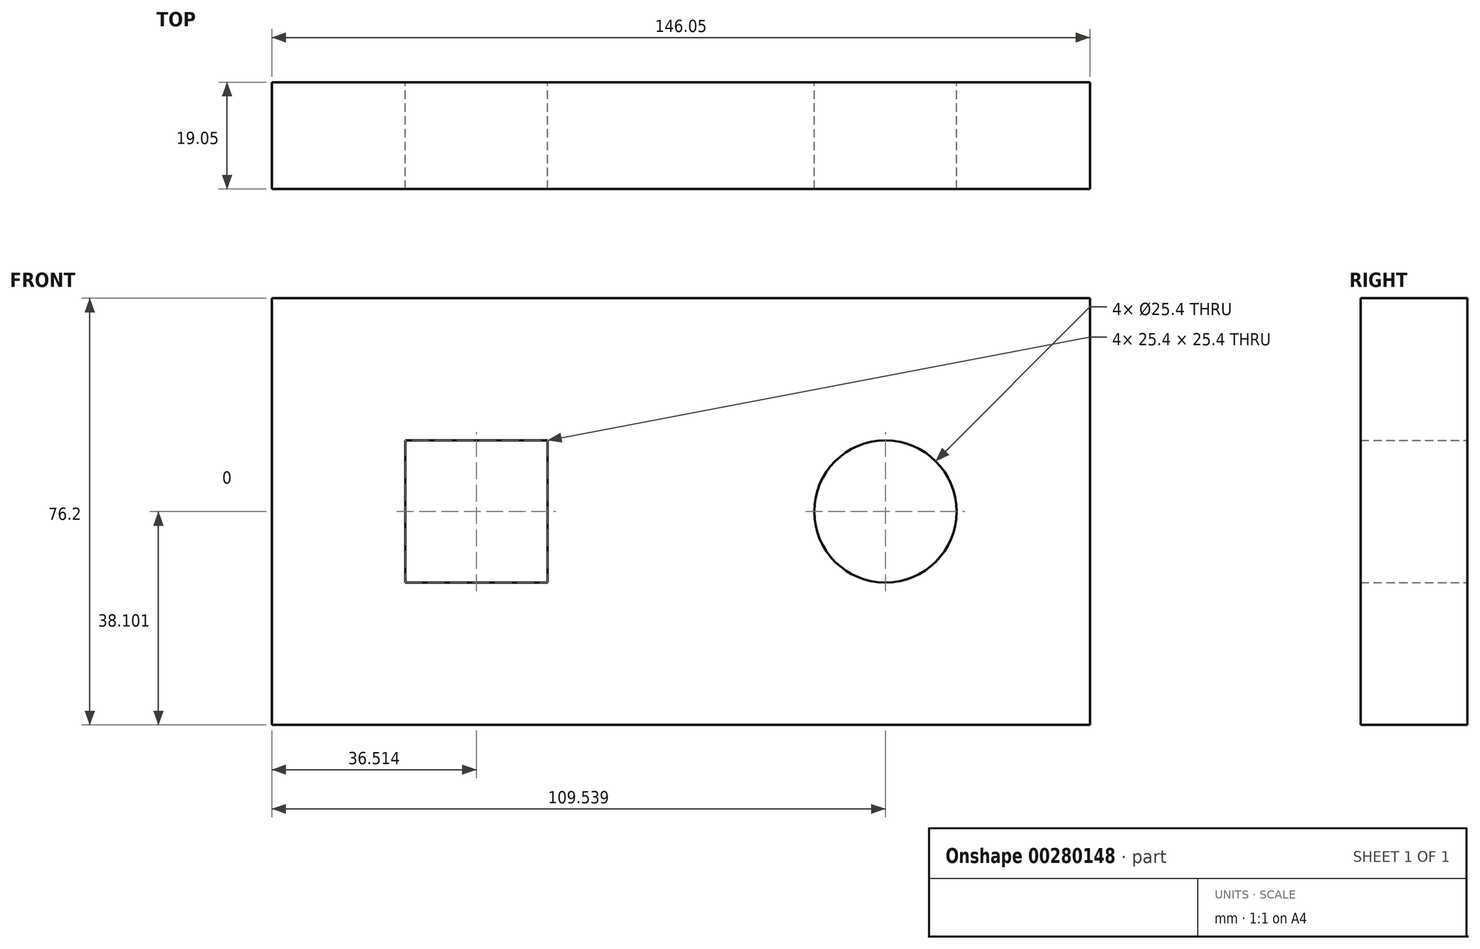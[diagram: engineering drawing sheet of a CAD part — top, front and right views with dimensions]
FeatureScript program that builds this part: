
annotation { "Feature Type Name" : "Feature", "Feature Type Description" : "" }
export const myFeature = defineFeature(function(context is Context, id is Id, definition is map)
    precondition{}
    {
        {
            var Q0;
            Q0=qCreatedBy(makeId("Front.planeOp"),FACE);
            var sketch = newSketch(context, id + "F0", { "sketchPlane" : qUnion([Q0])});
            skLineSegment(sketch, "E0.bottom", {"start": v(-79.16, 56) * mm, "end": v(66.9, 56) * mm});
            skLineSegment(sketch, "E0.top", {"start": v(-79.16, -20.2) * mm, "end": v(66.9, -20.2) * mm});
            skLineSegment(sketch, "E0.left", {"start": v(-79.16, 56) * mm, "end": v(-79.16, -20.2) * mm});
            skLineSegment(sketch, "E0.right", {"start": v(66.9, 56) * mm, "end": v(66.9, -20.2) * mm});
            skCircle(sketch, "E1", {"center": v(30.38, 17.9) * mm, "radius": 12.7 * mm});
            skLineSegment(sketch, "E2.bottom", {"start": v(-55.35, 30.6) * mm, "end": v(-29.95, 30.6) * mm});
            skLineSegment(sketch, "E2.top", {"start": v(-55.35, 5.2) * mm, "end": v(-29.95, 5.2) * mm});
            skLineSegment(sketch, "E2.left", {"start": v(-55.35, 30.6) * mm, "end": v(-55.35, 5.2) * mm});
            skLineSegment(sketch, "E2.right", {"start": v(-29.95, 30.6) * mm, "end": v(-29.95, 5.2) * mm});
            skSolve(sketch);
        }
        {
            var Q0;
            Q0=makeQuery(id+"F0.imprint","IMPRINT",FACE,{"disambiguationData":[TD([[makeQuery(id+"F0.imprint","IMPRINT",EDGE,{"derivedFrom":sQuery(id+"F0.wireOp",EDGE,"E0.bottom")}),-1.0]])]});
            extrude(context, id + "F1", {"entities" : qUnion([Q0]), "depth" : 19.05 * mm});
        }
    });
